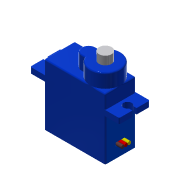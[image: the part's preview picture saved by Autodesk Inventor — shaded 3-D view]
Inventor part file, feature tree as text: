
AUTODESK INVENTOR PART (.ipt)
format: ipt  version: 2019 (Build 230136000, 136)  size: 289,792 bytes
history: native  units: mm
features: extrude x6, sketch x6, other x2, fillet x1, projected_geometry x1
ambient origin geometry x8: Origin, YZ Plane, XZ Plane, XY Plane, X Axis, Y Axis, Z Axis, Center Point
bodies: Body1 (feature_tree)
feature tree (16):
  other  "솔리드1"
  extrude  "돌출1"  Depth=11.0mm
  other  "작업 평면1"
  extrude  "돌출2"  Depth=22.0mm TaperAngle=0.0deg
  extrude  "돌출3"  [1 undecoded]
  fillet  "모깎기1"  Radius=5.0mm
  extrude  "돌출4"  Depth=5.0mm
  extrude  "돌출6"  Depth=3.0mm
  extrude  "Extrusion7"  Depth=3.0mm
  sketch  "스케치1"
  sketch  "스케치2"
  sketch  "스케치3"
  sketch  "스케치4"
  sketch  "스케치6"
  sketch  "Sketch7"  dims[d0=22.0mm d1=11.0mm d2=22.0mm d3=0.0mm d4=-15.0mm d5=5.0mm d6=5.0mm d7=3.0mm d8=2.5mm d9=1.5mm d10=2.0mm d11=0.0mm d12=6.0mm d13=5.0mm d14=5.0mm d15=0.0mm d16=0.5mm d17=4.5mm d18=3.0mm d19=0.0mm d25=1.2mm d26=3.6mm d27=5.0mm d28=1.0mm d29=0.0mm d30=1.2mm d31=1.2mm d32=1.2mm d33=3.0mm d34=0.0mm]
  projected_geometry  "Projected Loop1"
note: 1 required parameter value undecoded (feature->parameter linkage not recoverable at this tier; creation-order binding heuristic only, values carry confidence <= 0.55)
